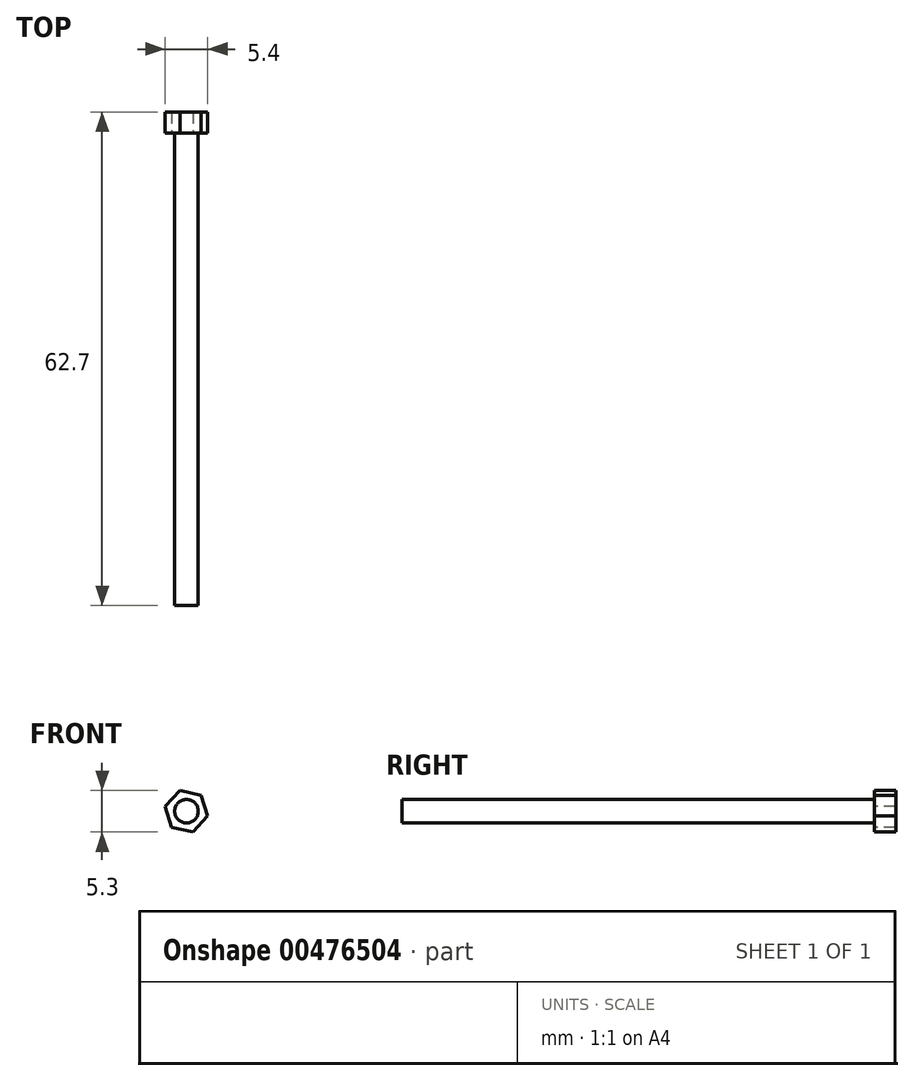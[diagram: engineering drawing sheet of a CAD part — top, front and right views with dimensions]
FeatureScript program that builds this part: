
annotation { "Feature Type Name" : "Feature", "Feature Type Description" : "" }
export const myFeature = defineFeature(function(context is Context, id is Id, definition is map)
    precondition{}
    {
        {
            var Q0;
            Q0=qCreatedBy(makeId("Front.planeOp"),FACE);
            var sketch = newSketch(context, id + "F0", { "sketchPlane" : qUnion([Q0])});
            skCircle(sketch, "E0", {"center": v(0, 0) * mm, "radius": 1.5 * mm});
            skCircle(sketch, "E1.cCircle", {"center": v(0, 0) * mm, "radius": 2.77 * mm, "construction": true});
            skLineSegment(sketch, "E1.0", {"start": v(-2.7, 0.6) * mm, "end": v(-0.82, 2.65) * mm});
            skLineSegment(sketch, "E1.1", {"start": v(-0.82, 2.65) * mm, "end": v(1.88, 2.04) * mm});
            skLineSegment(sketch, "E1.2", {"start": v(1.88, 2.04) * mm, "end": v(2.7, -0.6) * mm});
            skLineSegment(sketch, "E1.3", {"start": v(2.7, -0.6) * mm, "end": v(0.82, -2.65) * mm});
            skLineSegment(sketch, "E1.4", {"start": v(0.82, -2.65) * mm, "end": v(-1.88, -2.04) * mm});
            skLineSegment(sketch, "E1.5", {"start": v(-1.88, -2.04) * mm, "end": v(-2.7, 0.6) * mm});
            skSolve(sketch);
        }
        {
            var Q0;
            Q0=makeQuery(id+"F0.imprint","IMPRINT",FACE,{"disambiguationData":[TD([[makeQuery(id+"F0.imprint","IMPRINT",EDGE,{"derivedFrom":sQuery(id+"F0.wireOp",EDGE,"E0")}),1.0]])]});
            extrude(context, id + "F1", {"entities" : qUnion([Q0]), "depth" : 60 * mm, "offsetDistance" : 25 * mm});
        }
        {
            var Q0;
            Q0=makeQuery(id+"F0.imprint","IMPRINT",FACE,{"disambiguationData":[TD([[makeQuery(id+"F0.imprint","IMPRINT",EDGE,{"derivedFrom":sQuery(id+"F0.wireOp",EDGE,"E0")}),-1.0]])]});
            var Q1;
            Q1=makeQuery(id+"F0.imprint","IMPRINT",FACE,{"disambiguationData":[TD([[makeQuery(id+"F0.imprint","IMPRINT",EDGE,{"derivedFrom":sQuery(id+"F0.wireOp",EDGE,"E0")}),1.0]])]});
            extrude(context, id + "F2", {"entities" : qUnion([Q0, Q1]), "operationType" : NewBodyOperationType.ADD, "oppositeDirection" : true, "depth" : 2.7 * mm, "offsetDistance" : 25 * mm});
        }
    });
